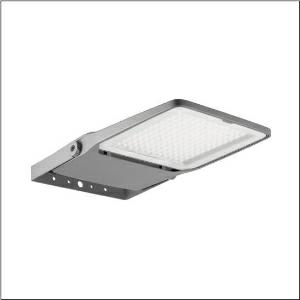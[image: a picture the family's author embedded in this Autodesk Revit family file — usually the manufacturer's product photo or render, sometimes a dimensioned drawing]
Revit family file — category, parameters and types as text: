
# Revit family: floodlight_fl_20_midi___pl61_5xa7682e2c2ac_53d1
name_source: partatom
category: Lighting Fixtures
units: mm (PartAtom-declared; Revit-internal decimal feet)

## family parameters
Cut with Voids When Loaded = No
Host = Face
Light Source = No
Part Type = Normal
Room Calculation Point = No
Round Connector Dimension = Use Diameter
Shared = No

## types (1)
- --- (1 x LED 4000K / CRI = 70 (unbekannt), 27150 lm, 4000K)
    Apparent Load = 208 VA
    CIE Flux Codes = 33 65 98 100 100
    Color Rendering = 70
    Color Temperature = 4000K
    Default Elevation = 1800 mm
    Description = Floodlight FL 20 midi, floodlight, primary light control with lens, of plastic, primary optical cover: protective disc, of toughened safety glass, transparent, light distribution: PL61, light emission: direct distribution, primary light characteristic: asymmetric, installation type: surface-mounted, LED High Power LED, rated luminous flux: 27.150 lm, light colour: 740, colour temperature: 4000K, control gear: ECG Plus, control: flexible luminous flux parameterisation, time-dependent luminous flux control, digital communication interface, power reduction, overheat protection, electronic power reduction, with terminal, 5-pole, max. 2.5mm², mains connection: 220..240V, AC, 50/60Hz, rated input power: 208W, LED unit, of diecast aluminium, powder-coated, Siteco® metallic grey (DB 702S), length: 731 mm, width: 450 mm, height: 76mm, housing frame, of diecast aluminium, powder-coated, Siteco® metallic grey (DB 702S), wall fastening, of steel, powder-coated, Siteco® metallic grey (DB 702S), DALIprotection rating (complete): IP66, insulation class (complete): insulation class II (safety insulation), certification: CE, ENEC, VDE, protection symbol: D, permissible ambient temperature for indoor applications: -40..+40°C, permissible ambient temperature for outdoor applications: -40..+50°C, standard: DIN EN 12944, packaging unit: 1 piece

Light Distribution: PL61
    Height = 76 mm
    Lamp = 1 x LED 4000K / CRI >= 70 (unbekannt)
    Lamp Light Flux = 27150 lm
    Lamp count = 1
    Length = 731 mm
    Luminous efficacy = 131 lm/W
    Manufacturer = Siteco
    ModVariant = No
    Model = 5XA7682E2C2AC
    Number of Poles = 1
    OnlyDefault = Yes
    Power Factor = 1
    Product Name = Floodlight FL 20 midi | PL61
    Product group = floodlight | pylon top
    ProductGroupID = 6101
    Protection Class = Protection class II
    Protection Degree = IP 66
    RLX_Detail_Level = 1
    RlxData = <blob elided: 92129 chars, md5=846aa81c>
    Socket = socket
    Standby Power = 0 W
    System Light Flux = 27150 lm
    System Power = 208 W
    Type Comments = factory setting: luminous flux: 100 % | dim-lin: 254 | 484 mA
    Type Image = l_1005944.jpg
    URL = http://relux.com
    VarID = @adj_142281
    Voltage = 0 V
    Weight = 0.00 kg
    Width = 450 mm

## geometry (parser evidence)
native form markers: Blend x4, Sweep x12
no freeform markers — native parametric forms only
